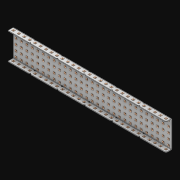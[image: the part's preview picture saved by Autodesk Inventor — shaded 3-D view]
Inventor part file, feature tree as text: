
AUTODESK INVENTOR PART (.ipt)
format: ipt  version: 2021 (Build 250183000, 183)  size: 3,730,944 bytes
history: native  units: in
note: dims shown in document units (in); Inventor stores cm internally (conversion verified against a paired STEP export)
features: extrude x204, other x203, sketch x4, thicken_offset x3, pattern_linear x3, imported_body x1
ambient origin geometry x8: Origin, YZ Plane, XZ Plane, XY Plane, X Axis, Y Axis, Z Axis, Center Point
bodies: Solid1 (feature_tree)
feature tree (418):
  thicken_offset  "Thicken1"
  thicken_offset  "Thicken2"
  thicken_offset  "Thicken3"
  pattern_linear  "Rectangular Pattern1"  Spacing1=0.001in  [1 undecoded]
  pattern_linear  "Rectangular Pattern2"  Spacing1=0.001in  [1 undecoded]
  pattern_linear  "Rectangular Pattern3"  Spacing1=0.182in  [1 undecoded]
  extrude  "Extrusion1"  Depth=0.063in TaperAngle=0.0deg
  sketch  "Sketch1"  dims[d0=0.001in]
  other  "Srf1"
  sketch  "Sketch2"  dims[d1=0.001in]
  other  "Srf2"
  sketch  "Sketch3"  dims[d2=0.001in]
  other  "Srf3"
  other  "Srf4"
  other  "Srf5"
  other  "Srf6"
  other  "Srf7"
  other  "Srf8"
  other  "Srf9"
  other  "Srf10"
  other  "Srf11"
  other  "Srf12"
  other  "Srf13"
  other  "Srf14"
  other  "Srf15"
  other  "Srf16"
  other  "Srf17"
  other  "Srf18"
  other  "Srf19"
  other  "Srf20"
  other  "Srf21"
  other  "Srf22"
  other  "Srf23"
  other  "Srf24"
  other  "Srf25"
  other  "Srf26"
  other  "Srf27"
  other  "Srf28"
  other  "Srf29"
  other  "Srf30"
  other  "Srf31"
  other  "Srf38"
  other  "Srf39"
  other  "Srf40"
  other  "Srf41"
  other  "Srf42"
  other  "Srf43"
  other  "Srf44"
  other  "Srf45"
  other  "Srf46"
  other  "Srf47"
  other  "Srf48"
  other  "Srf49"
  other  "Srf50"
  other  "Srf51"
  other  "Srf52"
  other  "Srf53"
  other  "Srf54"
  other  "Srf55"
  other  "Srf56"
  other  "Srf57"
  other  "Srf58"
  other  "Srf59"
  other  "Srf60"
  other  "Srf61"
  other  "Srf62"
  other  "Srf63"
  other  "Srf64"
  other  "Srf65"
  other  "Srf72"
  other  "Srf73"
  other  "Srf74"
  other  "Srf75"
  other  "Srf76"
  other  "Srf77"
  other  "Srf78"
  other  "Srf79"
  other  "Srf80"
  other  "Srf81"
  other  "Srf82"
  other  "Srf83"
  other  "Srf84"
  other  "Srf85"
  other  "Srf86"
  other  "Srf87"
  other  "Srf88"
  other  "Srf89"
  other  "Srf90"
  other  "Srf91"
  other  "Srf92"
  other  "Srf93"
  other  "Srf94"
  other  "Srf95"
  other  "Srf96"
  other  "Srf97"
  other  "Srf98"
  other  "Srf99"
  other  "Srf106"
  other  "Srf107"
  other  "Srf108"
  other  "Srf109"
  other  "Srf110"
  other  "Srf111"
  other  "Srf112"
  other  "Srf113"
  other  "Srf114"
  other  "Srf115"
  other  "Srf116"
  other  "Srf117"
  other  "Srf118"
  other  "Srf119"
  other  "Srf120"
  other  "Srf121"
  other  "Srf122"
  other  "Srf123"
  other  "Srf124"
  other  "Srf125"
  other  "Srf126"
  other  "Srf127"
  other  "Srf128"
  other  "Srf129"
  other  "Srf130"
  other  "Srf131"
  other  "Srf132"
  other  "Srf133"
  other  "Srf134"
  other  "Srf141"
  other  "Srf142"
  other  "Srf143"
  other  "Srf144"
  other  "Srf145"
  other  "Srf146"
  other  "Srf147"
  other  "Srf148"
  other  "Srf149"
  other  "Srf150"
  other  "Srf151"
  other  "Srf152"
  other  "Srf153"
  other  "Srf154"
  other  "Srf155"
  other  "Srf156"
  other  "Srf157"
  other  "Srf158"
  other  "Srf159"
  other  "Srf160"
  other  "Srf161"
  other  "Srf162"
  other  "Srf163"
  other  "Srf164"
  other  "Srf165"
  other  "Srf166"
  other  "Srf167"
  other  "Srf168"
  other  "Srf169"
  other  "Srf176"
  other  "Srf177"
  other  "Srf178"
  other  "Srf179"
  other  "Srf180"
  other  "Srf181"
  other  "Srf182"
  other  "Srf183"
  other  "Srf184"
  other  "Srf185"
  other  "Srf186"
  other  "Srf187"
  other  "Srf188"
  other  "Srf189"
  other  "Srf190"
  other  "Srf191"
  other  "Srf192"
  other  "Srf193"
  other  "Srf194"
  other  "Srf195"
  other  "Srf196"
  other  "Srf197"
  other  "Srf198"
  other  "Srf199"
  other  "Srf200"
  other  "Srf201"
  other  "Srf202"
  other  "Srf203"
  other  "Srf204"
  other  "Srf211"
  other  "Srf212"
  other  "Srf213"
  other  "Srf214"
  other  "Srf215"
  other  "Srf216"
  other  "Srf217"
  other  "Srf218"
  other  "Srf219"
  other  "Srf220"
  other  "Srf221"
  other  "Srf222"
  other  "Srf223"
  other  "Srf224"
  other  "Srf225"
  other  "Srf226"
  other  "Srf227"
  other  "Srf228"
  other  "Srf229"
  other  "Srf230"
  other  "Srf231"
  other  "Srf232"
  other  "Srf233"
  other  "Srf234"
  other  "Srf235"
  other  "Srf236"
  other  "Srf237"
  other  "Srf238"
  other  "Srf239"
  sketch  "Sketch4"  dims[d3=0.001in d4=0.001in d5=0.001in d6=0.182in d7=0.063in d8=0.0in d9=0.182in d10=0.063in d11=0.0in d12=0.182in d13=0.063in d14=0.0in d17=0.5in d18=11.4173in d20=0.5in d21=11.4173in d23=0.5in d24=1.9685in d26=0.5in d27=3.0in d28=0.0in]
  imported_body  "Imported1"
  extrude  "ExtrusionSrf1"  Depth=3.0in
  extrude  "ExtrusionSrf2"  Depth=0.063in TaperAngle=0.0deg
  extrude  "ExtrusionSrf3"  Depth=3.0in
  extrude  "ExtrusionSrf4"  Depth=0.063in TaperAngle=0.0deg
  extrude  "ExtrusionSrf5"  Depth=0.5in
  extrude  "ExtrusionSrf6"  Depth=3.0in
  extrude  "ExtrusionSrf7"  Depth=0.5in
  extrude  "ExtrusionSrf8"  Depth=3.0in
  extrude  "ExtrusionSrf9"  Depth=0.5in
  extrude  "ExtrusionSrf10"  Depth=0.5in
  extrude  "ExtrusionSrf11"  Depth=3.0in
  extrude  "ExtrusionSrf12"  TaperAngle=0.0deg  [1 undecoded]
  extrude  "ExtrusionSrf13"  [1 undecoded]
  extrude  "ExtrusionSrf14"  [1 undecoded]
  extrude  "ExtrusionSrf15"  [1 undecoded]
  extrude  "ExtrusionSrf16"  [1 undecoded]
  extrude  "ExtrusionSrf17"  [1 undecoded]
  extrude  "ExtrusionSrf18"  [1 undecoded]
  extrude  "ExtrusionSrf19"  [1 undecoded]
  extrude  "ExtrusionSrf20"  [1 undecoded]
  extrude  "ExtrusionSrf21"  [1 undecoded]
  extrude  "ExtrusionSrf22"  [1 undecoded]
  extrude  "ExtrusionSrf23"  [1 undecoded]
  extrude  "ExtrusionSrf24"  [1 undecoded]
  extrude  "ExtrusionSrf25"  [1 undecoded]
  extrude  "ExtrusionSrf26"  [1 undecoded]
  extrude  "ExtrusionSrf27"  [1 undecoded]
  extrude  "ExtrusionSrf28"  [1 undecoded]
  extrude  "ExtrusionSrf29"  [1 undecoded]
  extrude  "ExtrusionSrf30"  [1 undecoded]
  extrude  "ExtrusionSrf31"  [1 undecoded]
  extrude  "ExtrusionSrf38"  [1 undecoded]
  extrude  "ExtrusionSrf39"  [1 undecoded]
  extrude  "ExtrusionSrf40"  [1 undecoded]
  extrude  "ExtrusionSrf41"  [1 undecoded]
  extrude  "ExtrusionSrf42"  [1 undecoded]
  extrude  "ExtrusionSrf43"  [1 undecoded]
  extrude  "ExtrusionSrf44"  [1 undecoded]
  extrude  "ExtrusionSrf45"  [1 undecoded]
  extrude  "ExtrusionSrf46"  [1 undecoded]
  extrude  "ExtrusionSrf47"  [1 undecoded]
  extrude  "ExtrusionSrf48"  [1 undecoded]
  extrude  "ExtrusionSrf49"  [1 undecoded]
  extrude  "ExtrusionSrf50"  [1 undecoded]
  extrude  "ExtrusionSrf51"  [1 undecoded]
  extrude  "ExtrusionSrf52"  [1 undecoded]
  extrude  "ExtrusionSrf53"  [1 undecoded]
  extrude  "ExtrusionSrf54"  [1 undecoded]
  extrude  "ExtrusionSrf55"  [1 undecoded]
  extrude  "ExtrusionSrf56"  [1 undecoded]
  extrude  "ExtrusionSrf57"  [1 undecoded]
  extrude  "ExtrusionSrf58"  [1 undecoded]
  extrude  "ExtrusionSrf59"  [1 undecoded]
  extrude  "ExtrusionSrf60"  [1 undecoded]
  extrude  "ExtrusionSrf61"  [1 undecoded]
  extrude  "ExtrusionSrf62"  [1 undecoded]
  extrude  "ExtrusionSrf63"  [1 undecoded]
  extrude  "ExtrusionSrf64"  [1 undecoded]
  extrude  "ExtrusionSrf65"  [1 undecoded]
  extrude  "ExtrusionSrf72"  [1 undecoded]
  extrude  "ExtrusionSrf73"  [1 undecoded]
  extrude  "ExtrusionSrf74"  [1 undecoded]
  extrude  "ExtrusionSrf75"  [1 undecoded]
  extrude  "ExtrusionSrf76"  [1 undecoded]
  extrude  "ExtrusionSrf77"  [1 undecoded]
  extrude  "ExtrusionSrf78"  [1 undecoded]
  extrude  "ExtrusionSrf79"  [1 undecoded]
  extrude  "ExtrusionSrf80"  [1 undecoded]
  extrude  "ExtrusionSrf81"  [1 undecoded]
  extrude  "ExtrusionSrf82"  [1 undecoded]
  extrude  "ExtrusionSrf83"  [1 undecoded]
  extrude  "ExtrusionSrf84"  [1 undecoded]
  extrude  "ExtrusionSrf85"  [1 undecoded]
  extrude  "ExtrusionSrf86"  [1 undecoded]
  extrude  "ExtrusionSrf87"  [1 undecoded]
  extrude  "ExtrusionSrf88"  [1 undecoded]
  extrude  "ExtrusionSrf89"  [1 undecoded]
  extrude  "ExtrusionSrf90"  [1 undecoded]
  extrude  "ExtrusionSrf91"  [1 undecoded]
  extrude  "ExtrusionSrf92"  [1 undecoded]
  extrude  "ExtrusionSrf93"  [1 undecoded]
  extrude  "ExtrusionSrf94"  [1 undecoded]
  extrude  "ExtrusionSrf95"  [1 undecoded]
  extrude  "ExtrusionSrf96"  [1 undecoded]
  extrude  "ExtrusionSrf97"  [1 undecoded]
  extrude  "ExtrusionSrf98"  [1 undecoded]
  extrude  "ExtrusionSrf99"  [1 undecoded]
  extrude  "ExtrusionSrf106"  [1 undecoded]
  extrude  "ExtrusionSrf107"  [1 undecoded]
  extrude  "ExtrusionSrf108"  [1 undecoded]
  extrude  "ExtrusionSrf109"  [1 undecoded]
  extrude  "ExtrusionSrf110"  [1 undecoded]
  extrude  "ExtrusionSrf111"  [1 undecoded]
  extrude  "ExtrusionSrf112"  [1 undecoded]
  extrude  "ExtrusionSrf113"  [1 undecoded]
  extrude  "ExtrusionSrf114"  [1 undecoded]
  extrude  "ExtrusionSrf115"  [1 undecoded]
  extrude  "ExtrusionSrf116"  [1 undecoded]
  extrude  "ExtrusionSrf117"  [1 undecoded]
  extrude  "ExtrusionSrf118"  [1 undecoded]
  extrude  "ExtrusionSrf119"  [1 undecoded]
  extrude  "ExtrusionSrf120"  [1 undecoded]
  extrude  "ExtrusionSrf121"  [1 undecoded]
  extrude  "ExtrusionSrf122"  [1 undecoded]
  extrude  "ExtrusionSrf123"  [1 undecoded]
  extrude  "ExtrusionSrf124"  [1 undecoded]
  extrude  "ExtrusionSrf125"  [1 undecoded]
  extrude  "ExtrusionSrf126"  [1 undecoded]
  extrude  "ExtrusionSrf127"  [1 undecoded]
  extrude  "ExtrusionSrf128"  [1 undecoded]
  extrude  "ExtrusionSrf129"  [1 undecoded]
  extrude  "ExtrusionSrf130"  [1 undecoded]
  extrude  "ExtrusionSrf131"  [1 undecoded]
  extrude  "ExtrusionSrf132"  [1 undecoded]
  extrude  "ExtrusionSrf133"  [1 undecoded]
  extrude  "ExtrusionSrf134"  [1 undecoded]
  extrude  "ExtrusionSrf141"  [1 undecoded]
  extrude  "ExtrusionSrf142"  [1 undecoded]
  extrude  "ExtrusionSrf143"  [1 undecoded]
  extrude  "ExtrusionSrf144"  [1 undecoded]
  extrude  "ExtrusionSrf145"  [1 undecoded]
  extrude  "ExtrusionSrf146"  [1 undecoded]
  extrude  "ExtrusionSrf147"  [1 undecoded]
  extrude  "ExtrusionSrf148"  [1 undecoded]
  extrude  "ExtrusionSrf149"  [1 undecoded]
  extrude  "ExtrusionSrf150"  [1 undecoded]
  extrude  "ExtrusionSrf151"  [1 undecoded]
  extrude  "ExtrusionSrf152"  [1 undecoded]
  extrude  "ExtrusionSrf153"  [1 undecoded]
  extrude  "ExtrusionSrf154"  [1 undecoded]
  extrude  "ExtrusionSrf155"  [1 undecoded]
  extrude  "ExtrusionSrf156"  [1 undecoded]
  extrude  "ExtrusionSrf157"  [1 undecoded]
  extrude  "ExtrusionSrf158"  [1 undecoded]
  extrude  "ExtrusionSrf159"  [1 undecoded]
  extrude  "ExtrusionSrf160"  [1 undecoded]
  extrude  "ExtrusionSrf161"  [1 undecoded]
  extrude  "ExtrusionSrf162"  [1 undecoded]
  extrude  "ExtrusionSrf163"  [1 undecoded]
  extrude  "ExtrusionSrf164"  [1 undecoded]
  extrude  "ExtrusionSrf165"  [1 undecoded]
  extrude  "ExtrusionSrf166"  [1 undecoded]
  extrude  "ExtrusionSrf167"  [1 undecoded]
  extrude  "ExtrusionSrf168"  [1 undecoded]
  extrude  "ExtrusionSrf169"  [1 undecoded]
  extrude  "ExtrusionSrf176"  [1 undecoded]
  extrude  "ExtrusionSrf177"  [1 undecoded]
  extrude  "ExtrusionSrf178"  [1 undecoded]
  extrude  "ExtrusionSrf179"  [1 undecoded]
  extrude  "ExtrusionSrf180"  [1 undecoded]
  extrude  "ExtrusionSrf181"  [1 undecoded]
  extrude  "ExtrusionSrf182"  [1 undecoded]
  extrude  "ExtrusionSrf183"  [1 undecoded]
  extrude  "ExtrusionSrf184"  [1 undecoded]
  extrude  "ExtrusionSrf185"  [1 undecoded]
  extrude  "ExtrusionSrf186"  [1 undecoded]
  extrude  "ExtrusionSrf187"  [1 undecoded]
  extrude  "ExtrusionSrf188"  [1 undecoded]
  extrude  "ExtrusionSrf189"  [1 undecoded]
  extrude  "ExtrusionSrf190"  [1 undecoded]
  extrude  "ExtrusionSrf191"  [1 undecoded]
  extrude  "ExtrusionSrf192"  [1 undecoded]
  extrude  "ExtrusionSrf193"  [1 undecoded]
  extrude  "ExtrusionSrf194"  [1 undecoded]
  extrude  "ExtrusionSrf195"  [1 undecoded]
  extrude  "ExtrusionSrf196"  [1 undecoded]
  extrude  "ExtrusionSrf197"  [1 undecoded]
  extrude  "ExtrusionSrf198"  [1 undecoded]
  extrude  "ExtrusionSrf199"  [1 undecoded]
  extrude  "ExtrusionSrf200"  [1 undecoded]
  extrude  "ExtrusionSrf201"  [1 undecoded]
  extrude  "ExtrusionSrf202"  [1 undecoded]
  extrude  "ExtrusionSrf203"  [1 undecoded]
  extrude  "ExtrusionSrf204"  [1 undecoded]
  extrude  "ExtrusionSrf211"  [1 undecoded]
  extrude  "ExtrusionSrf212"  [1 undecoded]
  extrude  "ExtrusionSrf213"  [1 undecoded]
  extrude  "ExtrusionSrf214"  [1 undecoded]
  extrude  "ExtrusionSrf215"  [1 undecoded]
  extrude  "ExtrusionSrf216"  [1 undecoded]
  extrude  "ExtrusionSrf217"  [1 undecoded]
  extrude  "ExtrusionSrf218"  [1 undecoded]
  extrude  "ExtrusionSrf219"  [1 undecoded]
  extrude  "ExtrusionSrf220"  [1 undecoded]
  extrude  "ExtrusionSrf221"  [1 undecoded]
  extrude  "ExtrusionSrf222"  [1 undecoded]
  extrude  "ExtrusionSrf223"  [1 undecoded]
  extrude  "ExtrusionSrf224"  [1 undecoded]
  extrude  "ExtrusionSrf225"  [1 undecoded]
  extrude  "ExtrusionSrf226"  [1 undecoded]
  extrude  "ExtrusionSrf227"  [1 undecoded]
  extrude  "ExtrusionSrf228"  [1 undecoded]
  extrude  "ExtrusionSrf229"  [1 undecoded]
  extrude  "ExtrusionSrf230"  [1 undecoded]
  extrude  "ExtrusionSrf231"  [1 undecoded]
  extrude  "ExtrusionSrf232"  [1 undecoded]
  extrude  "ExtrusionSrf233"  [1 undecoded]
  extrude  "ExtrusionSrf234"  [1 undecoded]
  extrude  "ExtrusionSrf235"  [1 undecoded]
  extrude  "ExtrusionSrf236"  [1 undecoded]
  extrude  "ExtrusionSrf237"  [1 undecoded]
  extrude  "ExtrusionSrf238"  [1 undecoded]
  extrude  "ExtrusionSrf239"  [1 undecoded]
note: 195 required parameter values undecoded (feature->parameter linkage not recoverable at this tier; creation-order binding heuristic only, values carry confidence <= 0.55)
